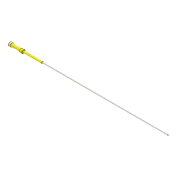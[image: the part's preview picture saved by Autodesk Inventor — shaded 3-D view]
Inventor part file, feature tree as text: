
AUTODESK INVENTOR PART (.ipt)
format: ipt  version: 2020.3 (Build 243373000, 373)  size: 129,024 bytes
history: native  units: mm
features: sketch x4, extrude x3, revolve x1, fillet x1, chamfer x1
ambient origin geometry x8: Origin, YZ Plane, XZ Plane, XY Plane, X Axis, Y Axis, Z Axis, Center Point
bodies: Body1 (feature_tree)
feature tree (10):
  revolve  "Umdrehung2"
  extrude  "Extrusion1"  Depth=2.5mm
  fillet  "Rundung1"  Radius=3.2mm
  extrude  "Extrusion2"  Depth=19.0mm
  extrude  "Extrusion3"  Depth=1.6mm
  chamfer  "Fase1"  Distance=0.5mm
  sketch  "Skizze2"  dims[d5=2.5mm d6=2.5mm d7=3.2mm]
  sketch  "Skizze3"  dims[d8=3.2mm d9=19.0mm]
  sketch  "Skizze4"  dims[d10=0.0mm d11=1.6mm]
  sketch  "Skizze5"  dims[d12=90.0deg d13=0.5mm d14=0.5mm d15=1.2mm d16=0.0mm d17=0.5mm d18=2.5mm d19=25.8mm d20=0.0mm d21=1.25mm d22=176.0mm d23=0.0mm d24=0.6mm d25=3.0mm d26=45.0deg]
